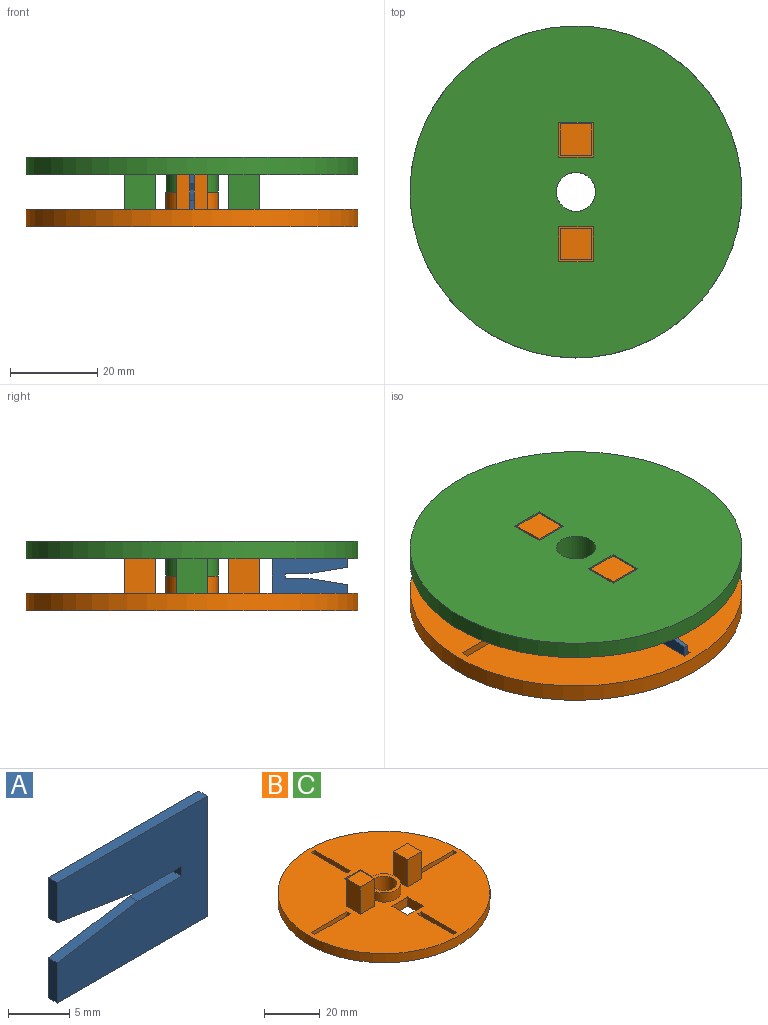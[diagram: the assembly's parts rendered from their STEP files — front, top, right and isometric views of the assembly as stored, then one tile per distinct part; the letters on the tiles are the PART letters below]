
ASSEMBLY  parts=3 mates=2
PART A: 12 faces, bbox 17.3x1x12 mm
  f0: plane 4x1mm, normal (-1,0,0), area 4mm2, adj f1,f9,f10,f11
  f1: plane 9.3x1.5mm, normal (-0.16,0,-0.99), area 9.4mm2, adj f0,f2,f10,f11
  f2: plane 5x1mm, normal (0,0,-1), area 5mm2, adj f1,f3,f10,f11
  f3: plane 1x1mm, normal (-1,0,0), area 1mm2, adj f2,f4,f10,f11
  f4: plane 5x1mm, normal (0,0,1), area 5mm2, adj f3,f5,f10,f11
  f5: plane 9.3x1.5mm, normal (-0.16,0,0.99), area 9.4mm2, adj f4,f6,f10,f11
  f6: plane 4x1mm, normal (-1,0,0), area 4mm2, adj f5,f7,f10,f11
  f7: plane 17.3x1mm, normal (0,0,-1), area 17.3mm2, adj f6,f8,f10,f11
  f8: plane 12x1mm, normal (1,0,0), area 12mm2, adj f7,f9,f10,f11
  f9: plane 17.3x1mm, normal (0,0,1), area 17.3mm2, adj f0,f8,f10,f11
  f10: plane 17.3x12mm, normal (0,-1,0), area 179.3mm2, adj f0,f1,f2,f3,f4,f5,f6,f7
  f11: plane 17.3x12mm, normal (0,1,0), area 179.3mm2, adj f0,f1,f2,f3,f4,f5,f6,f7
PART B: 44 faces, bbox 76.2x76.2x16 mm
  f0: plane 76.2x76.2mm, normal (0,0,1), area 4085.3mm2, adj f1,f4,f5,f6,f7,f8,f9,f10
  f1: cylinder r=38.1mm len=76.2mm, axis (0,0,-1), area 957.6mm2, adj f0,f2
  f2: plane 76.2x76.2mm, normal (0,0,-1), area 4368.8mm2, adj f1,f3,f4,f5,f6,f7,f8,f9
  f3: cylinder r=4.5mm len=9mm, axis (0,0,1), area 226.2mm2, adj f2,f23
  f4: plane 8x4mm, normal (-1,0,0), area 32mm2, adj f0,f2,f5,f7
  f5: plane 8x4mm, normal (0,-1,0), area 32mm2, adj f0,f2,f4,f6
  f6: plane 8x4mm, normal (1,0,0), area 32mm2, adj f0,f2,f5,f7
  f7: plane 8x4mm, normal (0,1,0), area 32mm2, adj f0,f2,f4,f6
  f8: plane 8x4mm, normal (0,-1,0), area 32mm2, adj f0,f2,f9,f11
  f9: plane 8x4mm, normal (1,0,0), area 32mm2, adj f0,f2,f8,f10
  f10: plane 8x4mm, normal (0,1,0), area 32mm2, adj f0,f2,f9,f11
  f11: plane 8x4mm, normal (-1,0,0), area 32mm2, adj f0,f2,f8,f10
  f12: plane 12x7.2mm, normal (1,0,0), area 86.4mm2, adj f0,f13,f15,f16
  f13: plane 12x7.2mm, normal (0,1,0), area 86.4mm2, adj f0,f12,f14,f16
  f14: plane 12x7.2mm, normal (-1,0,0), area 86.4mm2, adj f0,f13,f15,f16
  f15: plane 12x7.2mm, normal (0,-1,0), area 86.4mm2, adj f0,f12,f14,f16
  f16: plane 7.2x7.2mm, normal (0,0,1), area 51.8mm2, adj f12,f13,f14,f15
  f17: plane 12x7.2mm, normal (0,1,0), area 86.4mm2, adj f0,f18,f20,f21
  f18: plane 12x7.2mm, normal (-1,0,0), area 86.4mm2, adj f0,f17,f19,f21
  f19: plane 12x7.2mm, normal (0,-1,0), area 86.4mm2, adj f0,f18,f20,f21
  f20: plane 12x7.2mm, normal (1,0,0), area 86.4mm2, adj f0,f17,f19,f21
  f21: plane 7.2x7.2mm, normal (0,0,1), area 51.8mm2, adj f17,f18,f19,f20
  f22: cylinder r=6mm len=12mm, axis (0,0,-1), area 150.8mm2, adj f0,f23
  f23: plane 12x12mm, normal (0,0,1), area 49.5mm2, adj f3,f22
  f24: plane 2x1.8mm, normal (-1,0,0), area 3.6mm2, adj f0,f25,f27,f28
  f25: plane 18.1x2mm, normal (0,-1,0), area 36.2mm2, adj f0,f24,f26,f28
  f26: plane 2x1.8mm, normal (1,0,0), area 3.6mm2, adj f0,f25,f27,f28
  f27: plane 18.1x2mm, normal (0,1,0), area 36.2mm2, adj f0,f24,f26,f28
  f28: plane 18.1x1.8mm, normal (0,0,1), area 32.6mm2, adj f24,f25,f26,f27
  f29: plane 2x1.8mm, normal (0,1,0), area 3.6mm2, adj f0,f30,f32,f33
  f30: plane 18.1x2mm, normal (-1,0,0), area 36.2mm2, adj f0,f29,f31,f33
  f31: plane 2x1.8mm, normal (0,-1,0), area 3.6mm2, adj f0,f30,f32,f33
  f32: plane 18.1x2mm, normal (1,0,0), area 36.2mm2, adj f0,f29,f31,f33
  f33: plane 18.1x1.8mm, normal (0,0,1), area 32.6mm2, adj f29,f30,f31,f32
  f34: plane 2x1.8mm, normal (1,0,0), area 3.6mm2, adj f0,f35,f37,f38
  f35: plane 18.1x2mm, normal (0,1,0), area 36.2mm2, adj f0,f34,f36,f38
  f36: plane 2x1.8mm, normal (-1,0,0), area 3.6mm2, adj f0,f35,f37,f38
  f37: plane 18.1x2mm, normal (0,-1,0), area 36.2mm2, adj f0,f34,f36,f38
  f38: plane 18.1x1.8mm, normal (0,0,1), area 32.6mm2, adj f34,f35,f36,f37
  f39: plane 2x1.8mm, normal (0,1,0), area 3.6mm2, adj f0,f40,f42,f43
  f40: plane 18.1x2mm, normal (-1,0,0), area 36.2mm2, adj f0,f39,f41,f43
  f41: plane 2x1.8mm, normal (0,-1,0), area 3.6mm2, adj f0,f40,f42,f43
  f42: plane 18.1x2mm, normal (1,0,0), area 36.2mm2, adj f0,f39,f41,f43
  f43: plane 18.1x1.8mm, normal (0,0,1), area 32.6mm2, adj f39,f40,f41,f42
PART C: same geometry as B
PLACE A rot(axis=(0,0,1),90deg) t=(-33.04,-38.04,6.72)mm
PLACE B rot(axis=(0,0,-1),90deg) t=(-32.54,-19.64,-1.28)mm
PLACE C rot(axis=(1,0,0),180deg) t=(-32.54,-19.64,14.72)mm
MATE fastened B.f1 <-> C.f1  axis (0,0,1) through (-32.54,-19.64,6.72)mm
MATE fastened A.f9 <-> C.f43  axis (0,0,1) through (-32.54,-46.69,12.72)mm
